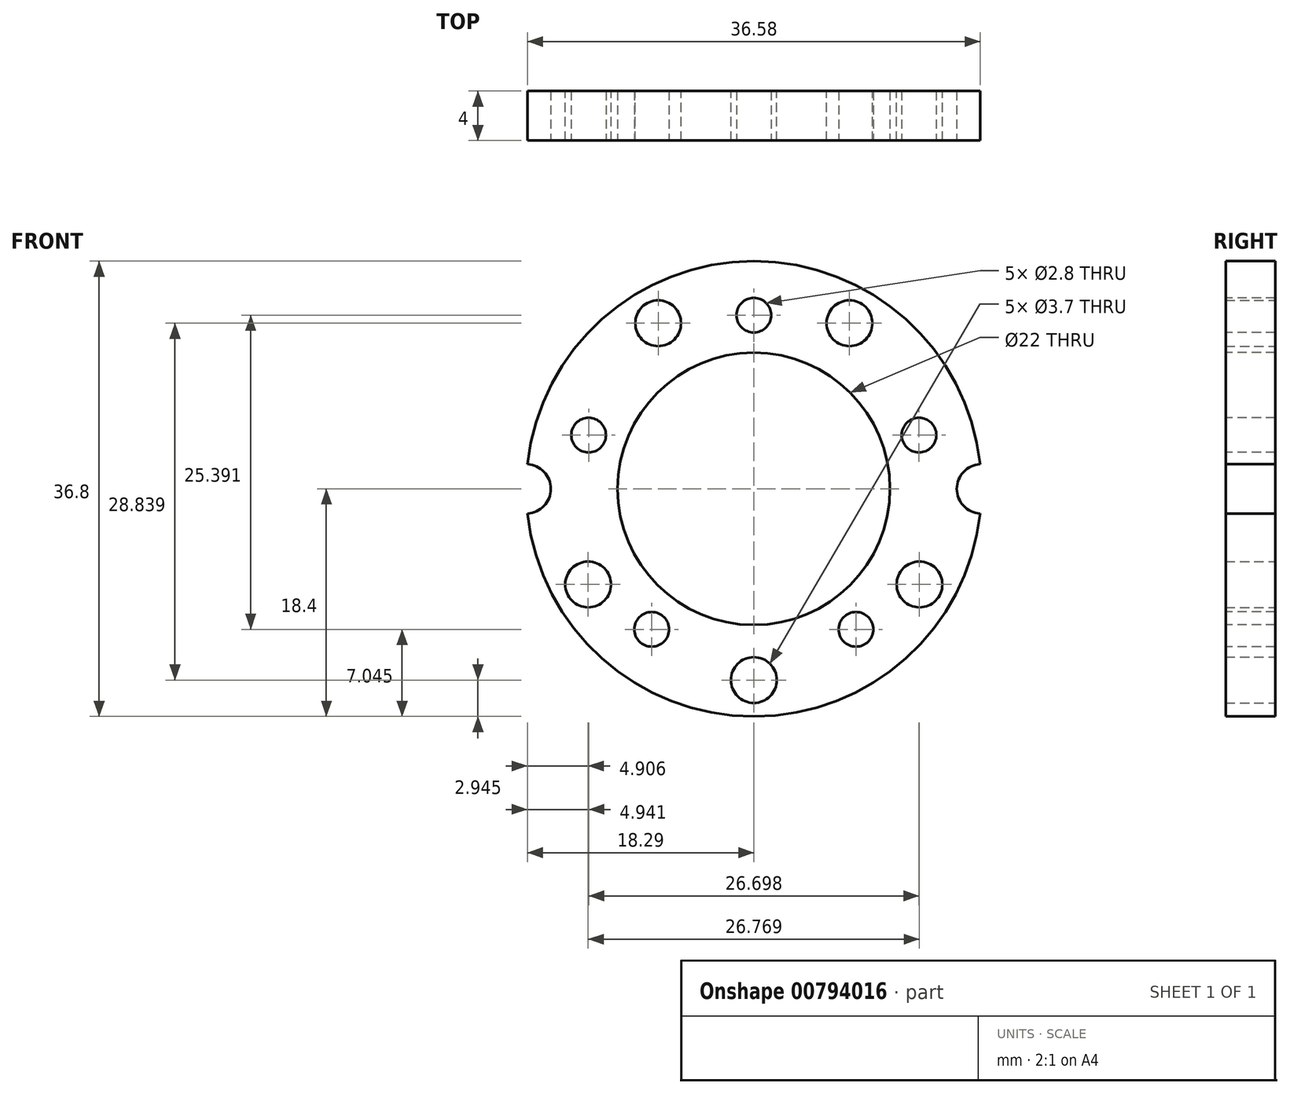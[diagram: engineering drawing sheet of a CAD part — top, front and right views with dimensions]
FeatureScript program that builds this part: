
annotation { "Feature Type Name" : "Feature", "Feature Type Description" : "" }
export const myFeature = defineFeature(function(context is Context, id is Id, definition is map)
    precondition{}
    {
        {
            var Q0;
            Q0=qCreatedBy(makeId("Front.planeOp"),FACE);
            var sketch = newSketch(context, id + "F0", { "sketchPlane" : qUnion([Q0])});
            skCircle(sketch, "E0", {"center": v(0, 0) * mm, "radius": 18.4 * mm});
            skCircle(sketch, "E1", {"center": v(0, 0) * mm, "radius": 11 * mm});
            skCircle(sketch, "E2.cCircle", {"center": v(0, 0) * mm, "radius": 14.04 * mm, "construction": true});
            skLineSegment(sketch, "E2.0", {"start": v(0, 14.04) * mm, "end": v(13.35, 4.34) * mm, "construction": true});
            skLineSegment(sketch, "E2.1", {"start": v(13.35, 4.34) * mm, "end": v(8.25, -11.36) * mm, "construction": true});
            skLineSegment(sketch, "E2.2", {"start": v(8.25, -11.36) * mm, "end": v(-8.25, -11.36) * mm, "construction": true});
            skLineSegment(sketch, "E2.3", {"start": v(-8.25, -11.36) * mm, "end": v(-13.35, 4.34) * mm, "construction": true});
            skLineSegment(sketch, "E2.4", {"start": v(-13.35, 4.34) * mm, "end": v(0, 14.04) * mm, "construction": true});
            skCircle(sketch, "E3", {"center": v(0, 14.04) * mm, "radius": 1.4 * mm});
            skCircle(sketch, "E4", {"center": v(13.35, 4.34) * mm, "radius": 1.4 * mm});
            skCircle(sketch, "E5", {"center": v(8.25, -11.36) * mm, "radius": 1.4 * mm});
            skCircle(sketch, "E6", {"center": v(-8.25, -11.36) * mm, "radius": 1.4 * mm});
            skCircle(sketch, "E7", {"center": v(-13.35, 4.34) * mm, "radius": 1.4 * mm});
            skSolve(sketch);
        }
        {
            var Q0;
            Q0=makeQuery(id+"F0.imprint","IMPRINT",FACE,{"disambiguationData":[TD([[makeQuery(id+"F0.imprint","IMPRINT",EDGE,{"derivedFrom":sQuery(id+"F0.wireOp",EDGE,"E0")}),1.0]])]});
            extrude(context, id + "F1", {"entities" : qUnion([Q0]), "oppositeDirection" : true, "depth" : 4 * mm, "offsetDistance" : 25 * mm});
        }
        {
            var Q0;
            Q0=makeQuery(id+"F1.opExtrude","CAP_FACE",FACE,{"disambiguationData":[OSD([sQuery(id+"F0.wireOp",EDGE,"E0"),sQuery(id+"F0.wireOp",EDGE,"E1"),sQuery(id+"F0.wireOp",EDGE,"E3"),sQuery(id+"F0.wireOp",EDGE,"E4"),sQuery(id+"F0.wireOp",EDGE,"E5"),sQuery(id+"F0.wireOp",EDGE,"E6"),sQuery(id+"F0.wireOp",EDGE,"E7")])],"isStart":false});
            var sketch = newSketch(context, id + "F2", { "sketchPlane" : qUnion([Q0])});
            skCircle(sketch, "E8.cCircle", {"center": v(0, 0) * mm, "radius": 15.45 * mm, "construction": true});
            skLineSegment(sketch, "E8.0", {"start": v(13.38, -7.73) * mm, "end": v(7.73, -13.38) * mm, "construction": true});
            skLineSegment(sketch, "E8.1", {"start": v(7.73, -13.38) * mm, "end": v(0, -15.45) * mm, "construction": true});
            skLineSegment(sketch, "E8.2", {"start": v(0, -15.45) * mm, "end": v(-7.73, -13.38) * mm, "construction": true});
            skLineSegment(sketch, "E8.3", {"start": v(-7.73, -13.38) * mm, "end": v(-13.38, -7.73) * mm, "construction": true});
            skLineSegment(sketch, "E8.4", {"start": v(-13.38, -7.73) * mm, "end": v(-15.45, 0) * mm, "construction": true});
            skLineSegment(sketch, "E8.5", {"start": v(-15.45, 0) * mm, "end": v(-13.38, 7.73) * mm, "construction": true});
            skLineSegment(sketch, "E8.6", {"start": v(-13.38, 7.73) * mm, "end": v(-7.73, 13.38) * mm, "construction": true});
            skLineSegment(sketch, "E8.7", {"start": v(-7.73, 13.38) * mm, "end": v(0, 15.45) * mm, "construction": true});
            skLineSegment(sketch, "E8.8", {"start": v(0, 15.45) * mm, "end": v(7.73, 13.38) * mm, "construction": true});
            skLineSegment(sketch, "E8.9", {"start": v(7.73, 13.38) * mm, "end": v(13.38, 7.73) * mm, "construction": true});
            skLineSegment(sketch, "E8.10", {"start": v(13.38, 7.73) * mm, "end": v(15.45, 0) * mm, "construction": true});
            skLineSegment(sketch, "E8.11", {"start": v(15.45, 0) * mm, "end": v(13.38, -7.73) * mm, "construction": true});
            skCircle(sketch, "E9", {"center": v(-13.38, 7.73) * mm, "radius": 1.85 * mm, "construction": true});
            skCircle(sketch, "E10", {"center": v(0, -15.45) * mm, "radius": 1.85 * mm});
            skCircle(sketch, "E11", {"center": v(13.38, 7.73) * mm, "radius": 1.85 * mm, "construction": true});
            skCircle(sketch, "E12", {"center": v(13.38, -7.73) * mm, "radius": 1.85 * mm});
            skCircle(sketch, "E13", {"center": v(-13.38, -7.73) * mm, "radius": 1.85 * mm});
            skCircle(sketch, "E14", {"center": v(-7.73, 13.38) * mm, "radius": 1.85 * mm});
            skCircle(sketch, "E15", {"center": v(7.73, 13.38) * mm, "radius": 1.85 * mm});
            skSolve(sketch);
        }
        {
            var Q0;
            Q0=qSketchRegion(id+"F2",true);
            extrude(context, id + "F3", {"entities" : qUnion([Q0]), "operationType" : NewBodyOperationType.REMOVE, "oppositeDirection" : true, "depth" : 25 * mm, "offsetDistance" : 25 * mm});
        }
        {
            var Q0;
            Q0=makeQuery(id+"F1.opExtrude","CAP_FACE",FACE,{"disambiguationData":[OSD([sQuery(id+"F0.wireOp",EDGE,"E0"),sQuery(id+"F0.wireOp",EDGE,"E1"),sQuery(id+"F0.wireOp",EDGE,"E3"),sQuery(id+"F0.wireOp",EDGE,"E4"),sQuery(id+"F0.wireOp",EDGE,"E5"),sQuery(id+"F0.wireOp",EDGE,"E6"),sQuery(id+"F0.wireOp",EDGE,"E7")])],"isStart":true});
            var sketch = newSketch(context, id + "F4", { "sketchPlane" : qUnion([Q0])});
            skCircle(sketch, "E16", {"center": v(-18.4, 0) * mm, "radius": 2 * mm});
            skCircle(sketch, "E17", {"center": v(18.4, 0) * mm, "radius": 2 * mm});
            skLineSegment(sketch, "E18", {"start": v(-18.4, 0) * mm, "end": v(18.4, 0) * mm, "construction": true});
            skSolve(sketch);
        }
        {
            var Q0;
            {var subQ0=sQuery(id+"F4.wireOp",EDGE,"E16");var subQ1=makeQuery(id+"F1.opExtrude","CAP_EDGE",EDGE,{"disambiguationData":[OSD([sQuery(id+"F0.wireOp",EDGE,"E0")])],"isStart":true});var subQ2=makeQuery(id+"F4.imprint","INTERSECT",VERTEX,{"disambiguationData":[OD(0.0)],"derivedFrom":[subQ1,subQ0]});Q0=makeQuery(id+"F4.imprint","IMPRINT",FACE,{"disambiguationData":[TD([[makeQuery(id+"F4.imprint","IMPRINT",EDGE,{"disambiguationData":[TD([[subQ2,-1.0]])],"derivedFrom":subQ0}),1.0]])]});}
            var Q1;
            {var subQ0=sQuery(id+"F4.wireOp",EDGE,"E17");var subQ1=makeQuery(id+"F1.opExtrude","CAP_EDGE",EDGE,{"disambiguationData":[OSD([sQuery(id+"F0.wireOp",EDGE,"E0")])],"isStart":true});var subQ2=makeQuery(id+"F4.imprint","INTERSECT",VERTEX,{"disambiguationData":[OD(0.0)],"derivedFrom":[subQ1,subQ0]});Q1=makeQuery(id+"F4.imprint","IMPRINT",FACE,{"disambiguationData":[TD([[makeQuery(id+"F4.imprint","IMPRINT",EDGE,{"disambiguationData":[TD([[subQ2,1.0]])],"derivedFrom":subQ0}),1.0]])]});}
            extrude(context, id + "F5", {"entities" : qUnion([Q0, Q1]), "operationType" : NewBodyOperationType.REMOVE, "oppositeDirection" : true, "depth" : 25 * mm, "offsetDistance" : 25 * mm});
        }
    });
